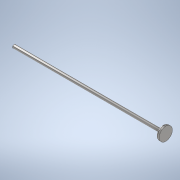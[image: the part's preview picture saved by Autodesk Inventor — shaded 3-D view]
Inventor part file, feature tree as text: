
AUTODESK INVENTOR PART (.ipt)
format: ipt  version: 2022 (Build 260153000, 153)  size: 113,664 bytes
history: native  units: in
note: dims shown in document units (in); Inventor stores cm internally (conversion verified against a paired STEP export)
features: extrude x2, fillet x2, sketch x2
ambient origin geometry x8: Origin, YZ Plane, XZ Plane, XY Plane, X Axis, Y Axis, Z Axis, Center Point
bodies: Solid1 (feature_tree)
feature tree (6):
  extrude  "Extrusion1"  Depth=35.4331in TaperAngle=0.0deg
  extrude  "Extrusion2"  Depth=0.7874in TaperAngle=0.0deg
  fillet  "Fillet1"  Radius=0.3937in
  fillet  "Fillet2"  Radius=0.3937in
  sketch  "Sketch1"  dims[d0=0.7874in d1=35.4331in d2=0.0in]
  sketch  "Sketch2"  dims[d3=3.1496in d4=0.7874in d5=0.0in d6=0.3937in d7=0.3937in]
